# Revit family: P190780JX-146c_JEF3115GS_StainlessSteel_JA_Cooking_Cooktops
name_source: partatom
category: Specialty Equipment
units: mm (PartAtom-declared; Revit-internal decimal feet)

## family parameters
Always vertical = Yes
Cut with Voids When Loaded = No
Enable Cutting in Views = No
Maintain Annotation Orientation = No
Part Type = Normal
Room Calculation Point = No
Round Connector Dimension = Use Diameter
Shared = No
Work Plane-Based = No

## types (1)
- JEF3115GS
    Amps = 15 A
    Body Material = ARCAT - Metal - Steel - Stainless
    Cooktop Material = ARCAT - Metal - Steel - Stainless
    Default Elevation = 0"
    Depth = 21"
    Description = Custom 15" Electric Griddle
Plaque chauffante électrique modulaire de 15 watts
    Dimension Guide = http://access.whirlpool.com Guide&sku=JEF3115GS&language=EN
http://access.whirlpool.com Guide&sku=JEF3115GS&language=EN
    Family Name = CUSTOMIZED COOKTOPS - 15"
    Feature 1 = 1,800-Watt Electric Griddle
Plaque chauffante électrique de 1800 watts
    Feature 2 = White LED Backlit Knobs
Boutons à base éclairée à DEL blanc
    Feature 3 = Low-Profile Design for Traditional Installations
Design à profil bas pour des installations traditionnelles
    Height = 7 21/32"
    Installation-Fabrication = http://access.whirlpool.com Instruction&sku=JEF3115GS&language=EN
http://access.whirlpool.com Instruction&sku=JEF3115GS&language=FR
    Knob Material = ARCAT - Metal - Steel - Gray
    Manufacturer = Jenn Air
    Model = JEF3115GS
    Voltage = 0 V
    Width = 15"

## geometry (parser evidence)
native form markers: Sweep x4
no freeform markers — native parametric forms only
